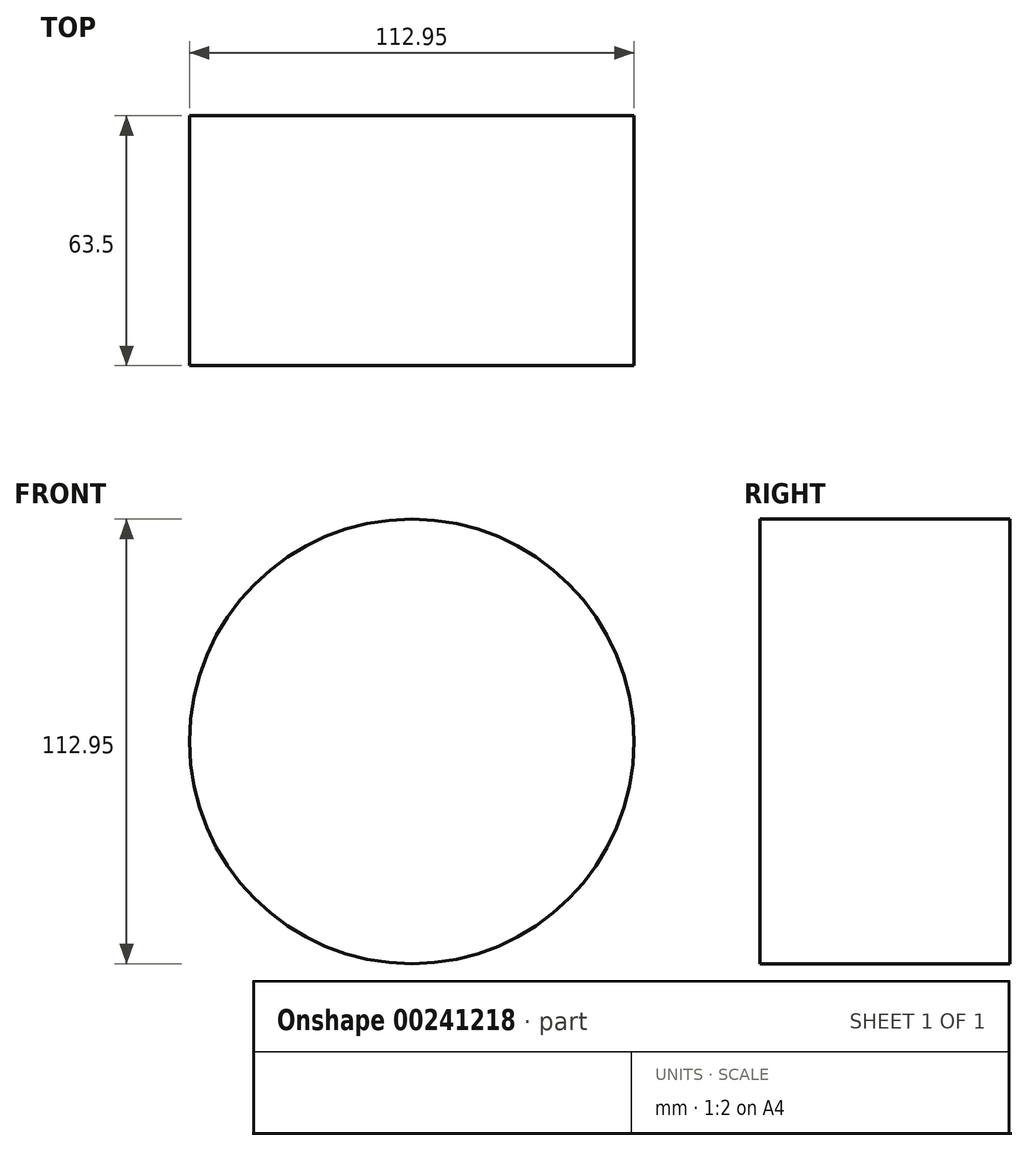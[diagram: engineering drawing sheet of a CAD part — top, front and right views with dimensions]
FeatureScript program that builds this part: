
annotation { "Feature Type Name" : "Feature", "Feature Type Description" : "" }
export const myFeature = defineFeature(function(context is Context, id is Id, definition is map)
    precondition{}
    {
        {
            var Q0;
            Q0=qCreatedBy(makeId("Front.planeOp"),FACE);
            var sketch = newSketch(context, id + "F0", { "sketchPlane" : qUnion([Q0])});
            skCircle(sketch, "E0", {"center": v(-3.35, -56.37) * mm, "radius": 56.47 * mm});
            skPoint(sketch, "E0.first.point", {"position": v(0, 0) * mm});
            skPoint(sketch, "E0.second.point", {"position": v(0, -112.75) * mm});
            skPoint(sketch, "E0.third.point", {"position": v(53, -59.96) * mm});
            skSolve(sketch);
        }
        {
            var Q0;
            Q0=makeQuery(id+"F0.imprint","IMPRINT",FACE,{"disambiguationData":[TD([[makeQuery(id+"F0.imprint","IMPRINT",EDGE,{"derivedFrom":sQuery(id+"F0.wireOp",EDGE,"E0")}),1.0]])]});
            extrude(context, id + "F1", {"entities" : qUnion([Q0]), "depth" : 63.5 * mm});
        }
    });
